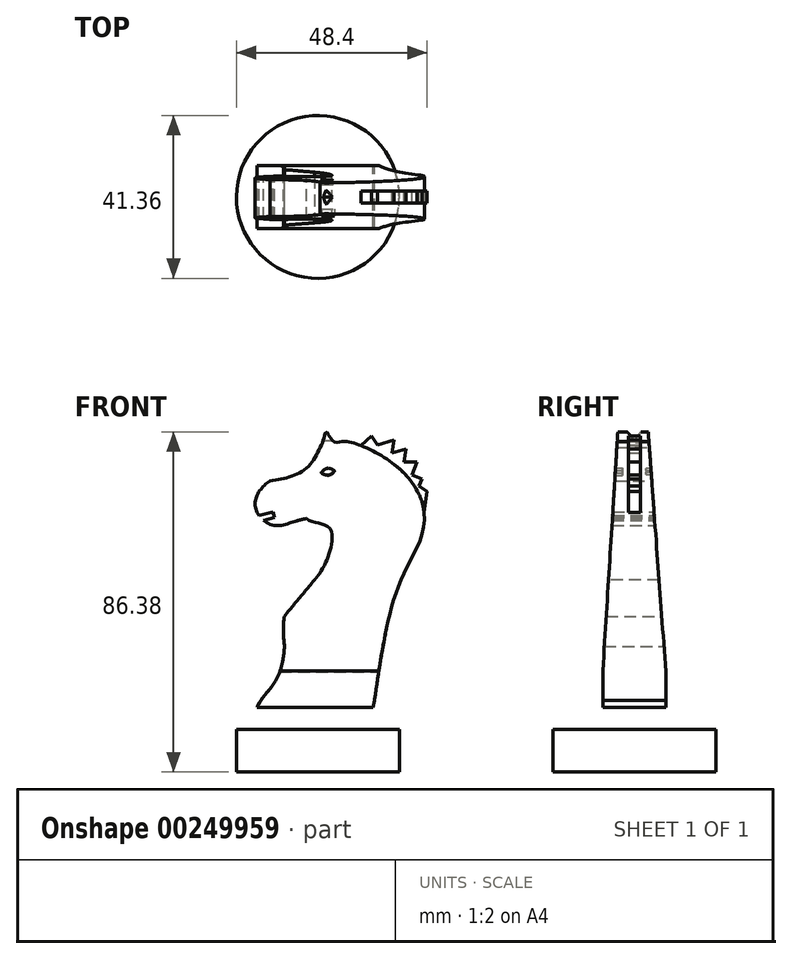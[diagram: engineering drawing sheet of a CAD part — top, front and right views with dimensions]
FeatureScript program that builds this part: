
annotation { "Feature Type Name" : "Feature", "Feature Type Description" : "" }
export const myFeature = defineFeature(function(context is Context, id is Id, definition is map)
    precondition{}
    {
        {
            var Q0;
            Q0=qCreatedBy(makeId("Front.planeOp"),FACE);
            var sketch = newSketch(context, id + "F0", { "sketchPlane" : qUnion([Q0])});
            skFitSpline(sketch, "E0", {"points": [v(14.4, -24.57) * mm, v(20.86, 5.43) * mm, v(26.92, 19.56) * mm, v(21.87, 33.15) * mm, v(6.44, 41.18) * mm, v(3.98, 41.11) * mm, v(2.15, 43.59) * mm, v(0.53, 39.66) * mm, v(-13.8, 29.8) * mm, v(-15.45, 23.2) * mm, v(-10.7, 19.79) * mm, v(-2.91, 21.57) * mm, v(6.28, 18.7) * mm, v(-14.26, -11.14) * mm, v(-15.47, -26.41) * mm], "startDerivative": vector(40.63, 279.81) * mm, "endDerivative": vector(86.1, -161.27) * mm});
            skLineSegment(sketch, "E1", {"start": v(-15.47, -26.41) * mm, "end": v(14.04, -26.41) * mm});
            skLineSegment(sketch, "E2", {"start": v(14.04, -26.41) * mm, "end": v(14.4, -24.57) * mm});
            skLineSegment(sketch, "E3.left", {"start": v(0, -26.41) * mm, "end": v(0, -42.79) * mm});
            skLineSegment(sketch, "E4", {"start": v(-15.47, -26.41) * mm, "end": v(0, -26.41) * mm});
            skPoint(sketch, "E5", {"position": v(2.36, 33.2) * mm});
            skLineSegment(sketch, "E6", {"start": v(10.99, 40.1) * mm, "end": v(13.6, 42.6) * mm});
            skLineSegment(sketch, "E7", {"start": v(13.6, 42.6) * mm, "end": v(15.12, 40.32) * mm});
            skLineSegment(sketch, "E8", {"start": v(15.12, 40.32) * mm, "end": v(19.4, 41.48) * mm});
            skLineSegment(sketch, "E9", {"start": v(19.4, 41.48) * mm, "end": v(18.78, 38.18) * mm});
            skLineSegment(sketch, "E10", {"start": v(18.78, 38.18) * mm, "end": v(22.43, 39.26) * mm});
            skLineSegment(sketch, "E11", {"start": v(22.43, 39.26) * mm, "end": v(21.93, 35.9) * mm});
            skLineSegment(sketch, "E12", {"start": v(21.93, 35.9) * mm, "end": v(25.21, 35.9) * mm});
            skLineSegment(sketch, "E13", {"start": v(25.21, 35.9) * mm, "end": v(23.95, 32.62) * mm});
            skLineSegment(sketch, "E14", {"start": v(23.95, 32.62) * mm, "end": v(26.42, 31.67) * mm});
            skLineSegment(sketch, "E15", {"start": v(26.42, 31.67) * mm, "end": v(25.72, 29.85) * mm});
            skLineSegment(sketch, "E16", {"start": v(25.72, 29.85) * mm, "end": v(25.34, 28.43) * mm});
            skLineSegment(sketch, "E17", {"start": v(25.72, 29.85) * mm, "end": v(27.72, 28.45) * mm});
            skLineSegment(sketch, "E18", {"start": v(27.72, 28.45) * mm, "end": v(26.98, 23.1) * mm});
            skLineSegment(sketch, "E19.bottom", {"start": v(-20.68, -42.79) * mm, "end": v(20.68, -42.79) * mm});
            skLineSegment(sketch, "E19.top", {"start": v(-20.68, -31.93) * mm, "end": v(20.68, -31.93) * mm});
            skLineSegment(sketch, "E19.left", {"start": v(-20.68, -42.79) * mm, "end": v(-20.68, -31.93) * mm});
            skLineSegment(sketch, "E19.right", {"start": v(20.68, -42.79) * mm, "end": v(20.68, -31.93) * mm});
            skPoint(sketch, "E19.middle", {"position": v(0, -37.36) * mm});
            skLineSegment(sketch, "E20", {"start": v(-15.47, -26.41) * mm, "end": v(-20.68, -31.93) * mm});
            skLineSegment(sketch, "E21", {"start": v(-14.95, 22.34) * mm, "end": v(-11.37, 23.2) * mm});
            skLineSegment(sketch, "E22", {"start": v(-11.37, 23.2) * mm, "end": v(-11.04, 21.82) * mm});
            skLineSegment(sketch, "E23", {"start": v(-11.04, 21.82) * mm, "end": v(-13.84, 21.15) * mm});
            skFitSpline(sketch, "E24", {"points": [v(-12.16, 31.13) * mm, v(-3.06, 34.28) * mm, v(0.53, 39.66) * mm], "startDerivative": vector(21.21, 2.49) * mm, "endDerivative": vector(5.53, 13.7) * mm});
            skFitSpline(sketch, "E25", {"points": [v(-2.91, 21.57) * mm, v(3.06, 19.04) * mm, v(-0.9, 5.94) * mm, v(-8.47, -10.86) * mm], "startDerivative": vector(21.49, -18.01) * mm, "endDerivative": vector(11.73, -98.74) * mm});
            skFitSpline(sketch, "E26", {"points": [v(-8.47, -10.86) * mm, v(-15.47, -26.41) * mm], "startDerivative": vector(-2.41, -32.24) * mm, "endDerivative": vector(-7, -15.56) * mm});
            skSolve(sketch);
        }
        {
            var Q0;
            Q0=makeQuery(id+"F0.imprint","IMPRINT",FACE,{"disambiguationData":[TD([[makeQuery(id+"F0.imprint","IMPRINT",EDGE,{"derivedFrom":sQuery(id+"F0.wireOp",EDGE,"E3.top")}),-1.0]])]});
            var Q1;
            {var subQ5=sQuery(id+"F0.wireOp",EDGE,"E19.left");Q1=makeQuery(id+"F0.imprint","IMPRINT",FACE,{"disambiguationData":[TD([[makeQuery(id+"F0.imprint","IMPRINT",EDGE,{"derivedFrom":subQ5}),-1.0]])]});}
            var Q2;
            {var subQ0=sQuery(id+"F0.wireOp",EDGE,"E4");Q2=makeQuery(id+"F0.imprint","IMPRINT",FACE,{"disambiguationData":[TD([[makeQuery(id+"F0.imprint","IMPRINT",EDGE,{"derivedFrom":subQ0}),-1.0]])]});}
            var Q3;
            Q3=sQuery(id+"F0.wireOp",EDGE,"E3.left");
            revolve(context, id + "F1", {"entities" : qUnion([Q0, Q1, Q2]), "axis" : qUnion([Q3]), "revolveType" : RevolveType.FULL});
        }
        {
            var Q0;
            {var subQ0=sQuery(id+"F0.wireOp",EDGE,"E0");Q0=makeQuery(id+"F0.imprint","IMPRINT",FACE,{"disambiguationData":[TD([[makeQuery(id+"F0.imprint","IMPRINT",EDGE,{"derivedFrom":subQ0}),1.0]])]});}
            var Q1;
            {var subQ0=sQuery(id+"F0.wireOp",EDGE,"E25");var subQ1=sQuery(id+"F0.wireOp",EDGE,"E0");var subQ2=makeQuery(id+"F0.imprint","INTERSECT",VERTEX,{"disambiguationData":[OD(0.0)],"derivedFrom":[subQ1,subQ0]});Q1=makeQuery(id+"F0.imprint","IMPRINT",FACE,{"disambiguationData":[TD([[makeQuery(id+"F0.imprint","IMPRINT",EDGE,{"disambiguationData":[TD([[subQ2,-1.0]])],"derivedFrom":subQ1}),-1.0]])]});}
            extrude(context, id + "F2", {"entities" : qUnion([Q0, Q1]), "operationType" : NewBodyOperationType.ADD, "depth" : 8 * mm, "hasSecondDirection" : true, "secondDirectionOppositeDirection" : true, "secondDirectionDepth" : 8 * mm});
        }
        {
            var Q0;
            Q0=makeQuery(id+"F2.opExtrude","CAP_FACE",FACE,{"disambiguationData":[OSD([sQuery(id+"F0.wireOp",EDGE,"E0"),sQuery(id+"F0.wireOp",EDGE,"E1"),sQuery(id+"F0.wireOp",EDGE,"E2"),sQuery(id+"F0.wireOp",EDGE,"E4")])],"isStart":false});
            var sketch = newSketch(context, id + "F3", { "sketchPlane" : qUnion([Q0])});
            skPoint(sketch, "E27", {"position": v(2.19, 33.22) * mm});
            skFitSpline(sketch, "E28", {"points": [v(0.9, 33.08) * mm, v(4.23, 33.64) * mm], "startDerivative": vector(2.5, 5) * mm, "endDerivative": vector(3.22, -2.98) * mm});
            skFitSpline(sketch, "E29", {"points": [v(4.23, 33.64) * mm, v(0.9, 33.08) * mm], "startDerivative": vector(-3.1, -4.17) * mm, "endDerivative": vector(-4.77, 2.03) * mm});
            skSolve(sketch);
        }
        {
            var Q0;
            Q0=sQuery(id+"F3.wireOp",VERTEX,"E27");
            var Q1;
            Q1=makeQuery(id+"F1.opRevolve","SWEPT_BODY",BODY,{"disambiguationData":[OSD([sQuery(id+"F0.wireOp",EDGE,"E3.top"),sQuery(id+"F0.wireOp",EDGE,"E3.left"),sQuery(id+"F0.wireOp",EDGE,"fb0f8cab-7311-4337-94df-a58856d9329e"),sQuery(id+"F0.wireOp",EDGE,"E4")])]});
            hole(context, id + "F4", {"style" : HoleStyle.SIMPLE, "endStyle" : HoleEndStyle.BLIND, "holeDiameter" : 2 * mm, "holeDepth" : 0.02 * mm, "tappedDepth" : 12 * mm, "tapClearance" : 3, "locations" : qUnion([Q0]), "scope" : qUnion([Q1])});
        }
        {
            var Q0;
            Q0=makeQuery(id+"F2.opExtrude","CAP_FACE",FACE,{"disambiguationData":[OSD([sQuery(id+"F0.wireOp",EDGE,"E0"),sQuery(id+"F0.wireOp",EDGE,"E1"),sQuery(id+"F0.wireOp",EDGE,"E2"),sQuery(id+"F0.wireOp",EDGE,"E4")])],"isStart":true});
            var sketch = newSketch(context, id + "F5", { "sketchPlane" : qUnion([Q0])});
            skPoint(sketch, "E30", {"position": v(-2.37, 33.35) * mm});
            skFitSpline(sketch, "E31", {"points": [v(-3.84, 33.74) * mm, v(-1.13, 33.85) * mm, v(-0.65, 33.35) * mm], "startDerivative": vector(7, 4.82) * mm, "endDerivative": vector(2.87, -2.98) * mm});
            skFitSpline(sketch, "E32", {"points": [v(-3.84, 33.74) * mm, v(-0.65, 33.35) * mm], "startDerivative": vector(1.88, -3.27) * mm, "endDerivative": vector(4.62, 3.12) * mm});
            skSolve(sketch);
        }
        {
            var Q0;
            Q0=makeQuery(id+"F5.imprint","IMPRINT",FACE,{"disambiguationData":[TD([[makeQuery(id+"F5.imprint","IMPRINT",EDGE,{"derivedFrom":sQuery(id+"F5.wireOp",EDGE,"E31")}),-1.0]])]});
            extrude(context, id + "F6", {"entities" : qUnion([Q0]), "operationType" : NewBodyOperationType.REMOVE, "oppositeDirection" : true, "depth" : 5 * mm});
        }
        {
            var Q0;
            Q0=qCreatedBy(makeId("Right.planeOp"),FACE);
            var sketch = newSketch(context, id + "F7", { "sketchPlane" : qUnion([Q0])});
            skPoint(sketch, "E33.middle", {"position": v(0, 43.2) * mm});
            skLineSegment(sketch, "E34", {"start": v(3.18, 48.16) * mm, "end": v(8.6, -25.5) * mm});
            skLineSegment(sketch, "E35", {"start": v(8.6, -25.5) * mm, "end": v(28.9, -21.44) * mm});
            skLineSegment(sketch, "E36", {"start": v(28.9, -21.44) * mm, "end": v(23.5, 51.9) * mm});
            skLineSegment(sketch, "E37", {"start": v(23.5, 51.9) * mm, "end": v(3.18, 48.16) * mm});
            skLineSegment(sketch, "E38", {"start": v(-3.92, 48.16) * mm, "end": v(-18.91, 50.77) * mm});
            skLineSegment(sketch, "E39", {"start": v(-18.91, 50.77) * mm, "end": v(-18.91, -18.74) * mm});
            skLineSegment(sketch, "E40", {"start": v(-18.91, -18.74) * mm, "end": v(-8.53, -25.5) * mm});
            skLineSegment(sketch, "E41", {"start": v(-8.53, -25.5) * mm, "end": v(-3.92, 48.16) * mm});
            skLineSegment(sketch, "E42", {"start": v(2.66, 45) * mm, "end": v(0, 41.38) * mm});
            skLineSegment(sketch, "E43", {"start": v(0, 41.38) * mm, "end": v(-2.92, 45) * mm});
            skLineSegment(sketch, "E44", {"start": v(-2.92, 45) * mm, "end": v(2.66, 45) * mm});
            skPoint(sketch, "E45", {"position": v(-1.46, 43.2) * mm});
            skSolve(sketch);
        }
        {
            var Q0;
            Q0 = qSketchRegion(id + "F7", true);
            extrude(context, id + "F8", {"entities" : qUnion([Q0]), "operationType" : NewBodyOperationType.REMOVE, "endBound" : BoundingType.SYMMETRIC, "oppositeDirection" : true, "depth" : 100 * mm});
        }
        {
            var Q0;
            Q0=makeQuery(id+"F3.imprint","IMPRINT",FACE,{"disambiguationData":[TD([[makeQuery(id+"F3.imprint","IMPRINT",EDGE,{"derivedFrom":sQuery(id+"F3.wireOp",EDGE,"E28")}),-1.0]])]});
            extrude(context, id + "F9", {"entities" : qUnion([Q0]), "operationType" : NewBodyOperationType.REMOVE, "oppositeDirection" : true, "depth" : 5 * mm});
        }
        {
            var Q0;
            {var subQ0=sQuery(id+"F0.wireOp",EDGE,"E6");Q0=makeQuery(id+"F0.imprint","IMPRINT",FACE,{"disambiguationData":[TD([[makeQuery(id+"F0.imprint","IMPRINT",EDGE,{"derivedFrom":subQ0}),-1.0]])]});}
            var Q1;
            {var subQ0=sQuery(id+"F0.wireOp",EDGE,"E16");Q1=makeQuery(id+"F0.imprint","IMPRINT",FACE,{"disambiguationData":[TD([[makeQuery(id+"F0.imprint","IMPRINT",EDGE,{"derivedFrom":subQ0}),1.0]])]});}
            extrude(context, id + "F10", {"entities" : qUnion([Q0, Q1]), "operationType" : NewBodyOperationType.ADD, "endBound" : BoundingType.SYMMETRIC, "depth" : 3 * mm});
        }
    });
